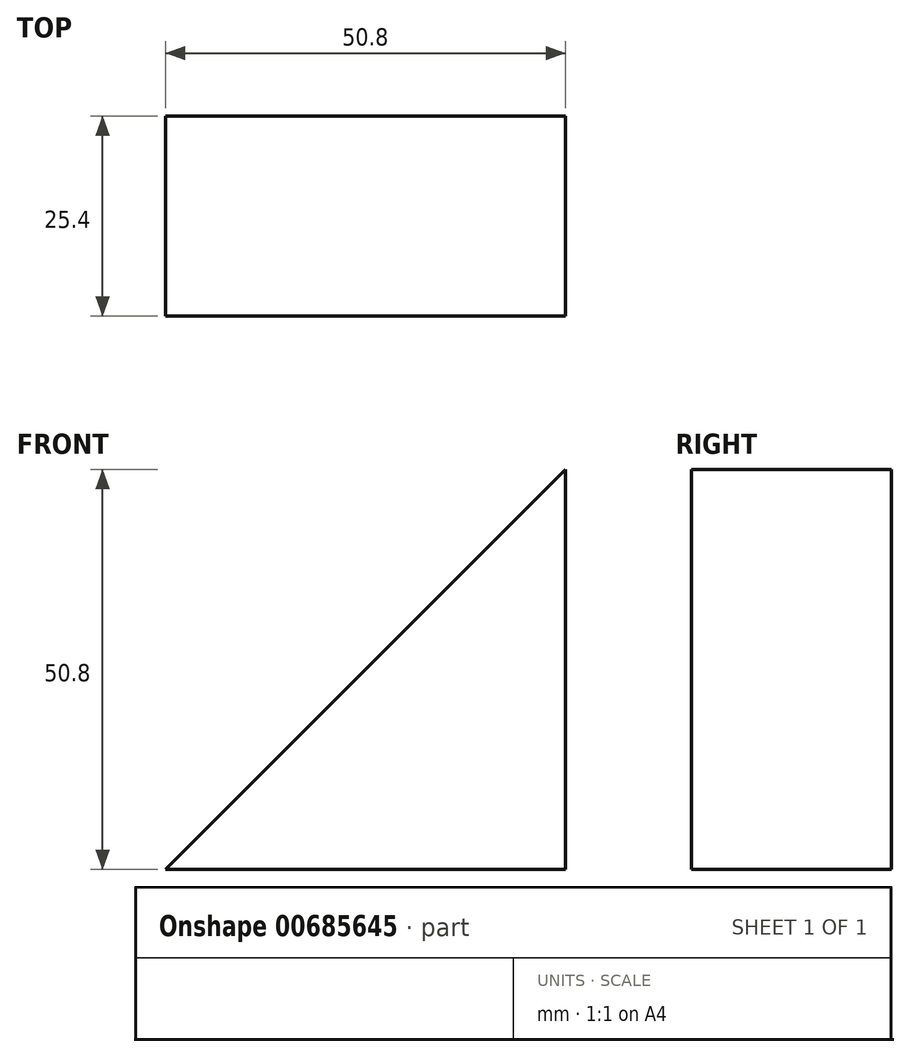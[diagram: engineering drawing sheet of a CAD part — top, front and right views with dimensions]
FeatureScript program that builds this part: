
annotation { "Feature Type Name" : "Feature", "Feature Type Description" : "" }
export const myFeature = defineFeature(function(context is Context, id is Id, definition is map)
    precondition{}
    {
        {
            var Q0;
            Q0=qCreatedBy(makeId("Front.planeOp"),FACE);
            var sketch = newSketch(context, id + "F0", { "sketchPlane" : qUnion([Q0])});
            skLineSegment(sketch, "E0", {"start": v(0, 0) * mm, "end": v(-50.8, 0) * mm});
            skLineSegment(sketch, "E1", {"start": v(0, 0) * mm, "end": v(0, 50.8) * mm});
            skLineSegment(sketch, "E2", {"start": v(0, 50.8) * mm, "end": v(-50.8, 0) * mm});
            skSolve(sketch);
        }
        {
            var Q0;
            Q0 = qSketchRegion(id + "F0", true);
            extrude(context, id + "F1", {"entities" : qUnion([Q0]), "depth" : 25.4 * mm, "offsetDistance" : 25.4 * mm});
        }
    });
